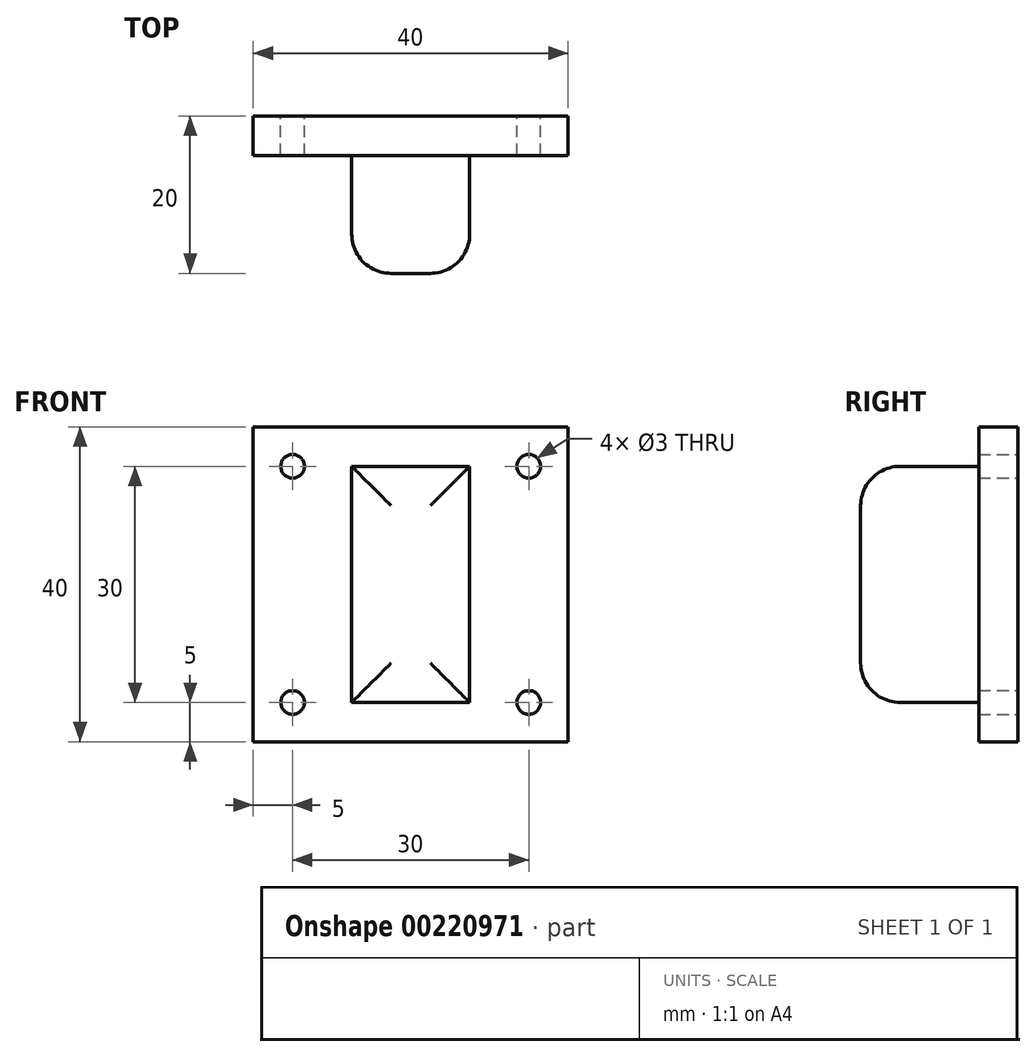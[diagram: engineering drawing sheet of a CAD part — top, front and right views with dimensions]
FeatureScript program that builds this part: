
annotation { "Feature Type Name" : "Feature", "Feature Type Description" : "" }
export const myFeature = defineFeature(function(context is Context, id is Id, definition is map)
    precondition{}
    {
        {
            var Q0;
            Q0=qCreatedBy(makeId("Front.planeOp"),FACE);
            var sketch = newSketch(context, id + "F0", { "sketchPlane" : qUnion([Q0])});
            skLineSegment(sketch, "E0", {"start": v(0, 0) * mm, "end": v(0, 15) * mm});
            skLineSegment(sketch, "E1", {"start": v(15, -15) * mm, "end": v(-15, -15) * mm});
            skCircle(sketch, "E2", {"center": v(-15, 15) * mm, "radius": 1.5 * mm});
            skCircle(sketch, "E3", {"center": v(15, 15) * mm, "radius": 1.5 * mm});
            skCircle(sketch, "E4", {"center": v(15, -15) * mm, "radius": 1.5 * mm});
            skCircle(sketch, "E5", {"center": v(-15, -15) * mm, "radius": 1.5 * mm});
            skLineSegment(sketch, "E6", {"start": v(0, 0) * mm, "end": v(-20, 0) * mm});
            skLineSegment(sketch, "E7", {"start": v(-20, 0) * mm, "end": v(-20, 20) * mm});
            skLineSegment(sketch, "E8.bottom", {"start": v(-20, 20) * mm, "end": v(20, 20) * mm});
            skLineSegment(sketch, "E8.top", {"start": v(-20, -20) * mm, "end": v(20, -20) * mm});
            skLineSegment(sketch, "E8.left", {"start": v(-20, 20) * mm, "end": v(-20, -20) * mm});
            skLineSegment(sketch, "E8.right", {"start": v(20, 20) * mm, "end": v(20, -20) * mm});
            skSolve(sketch);
        }
        {
            var Q0;
            Q0 = qSketchRegion(id + "F0", true);
            extrude(context, id + "F1", {"entities" : qUnion([Q0]), "depth" : 5 * mm, "offsetDistance" : 25 * mm});
        }
        {
            var Q0;
            Q0=makeQuery(id+"F1.opExtrude","CAP_FACE",FACE,{"disambiguationData":[OSD([sQuery(id+"F0.wireOp",EDGE,"E2"),sQuery(id+"F0.wireOp",EDGE,"E3"),sQuery(id+"F0.wireOp",EDGE,"E4"),sQuery(id+"F0.wireOp",EDGE,"E5"),sQuery(id+"F0.wireOp",EDGE,"E8.bottom"),sQuery(id+"F0.wireOp",EDGE,"E8.top"),sQuery(id+"F0.wireOp",EDGE,"E8.left"),sQuery(id+"F0.wireOp",EDGE,"E8.right")])],"isStart":false});
            var sketch = newSketch(context, id + "F2", { "sketchPlane" : qUnion([Q0])});
            skLineSegment(sketch, "E9", {"start": v(0, 0) * mm, "end": v(0, 15) * mm});
            skLineSegment(sketch, "E10", {"start": v(0, 15) * mm, "end": v(-7.5, 15) * mm});
            skLineSegment(sketch, "E11", {"start": v(-7.5, 15) * mm, "end": v(-7.5, -15) * mm});
            skLineSegment(sketch, "E12", {"start": v(-7.5, -15) * mm, "end": v(7.5, -15) * mm});
            skLineSegment(sketch, "E13", {"start": v(7.5, -15) * mm, "end": v(7.5, 15) * mm});
            skLineSegment(sketch, "E14", {"start": v(7.5, 15) * mm, "end": v(0, 15) * mm});
            skSolve(sketch);
        }
        {
            var Q0;
            Q0 = qSketchRegion(id + "F2", true);
            extrude(context, id + "F3", {"entities" : qUnion([Q0]), "operationType" : NewBodyOperationType.ADD, "depth" : 15 * mm, "offsetDistance" : 25 * mm});
        }
        {
            var Q0;
            Q0=makeQuery(id+"F3.opExtrude","CAP_EDGE",EDGE,{"disambiguationData":[OSD([sQuery(id+"F2.wireOp",EDGE,"E11")])],"isStart":false});
            var Q1;
            Q1=makeQuery(id+"F3.opExtrude","CAP_EDGE",EDGE,{"disambiguationData":[OSD([sQuery(id+"F2.wireOp",EDGE,"E10"),sQuery(id+"F2.wireOp",EDGE,"E14")])],"isStart":false});
            var Q2;
            Q2=makeQuery(id+"F3.opExtrude","CAP_EDGE",EDGE,{"disambiguationData":[OSD([sQuery(id+"F2.wireOp",EDGE,"E13")])],"isStart":false});
            var Q3;
            Q3=makeQuery(id+"F3.opExtrude","CAP_EDGE",EDGE,{"disambiguationData":[OSD([sQuery(id+"F2.wireOp",EDGE,"E12")])],"isStart":false});
            fillet(context, id + "F4", {"entities" : qUnion([Q0, Q1, Q2, Q3]), "radius" : 5 * mm, "tangentPropagation" : true, "allowEdgeOverflow" : false});
        }
    });
